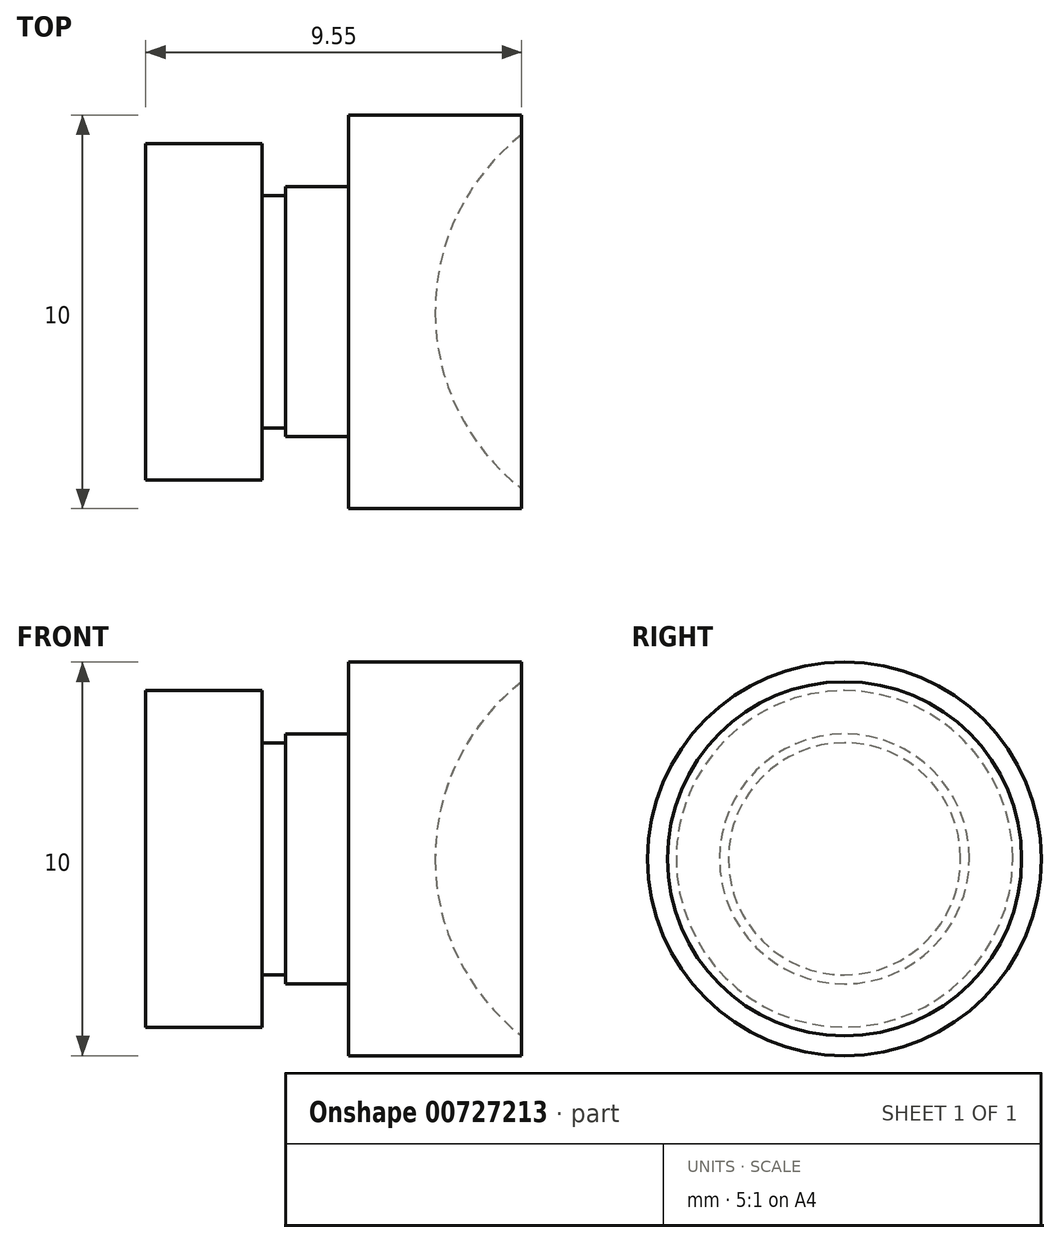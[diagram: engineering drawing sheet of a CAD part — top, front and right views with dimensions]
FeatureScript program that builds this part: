
annotation { "Feature Type Name" : "Feature", "Feature Type Description" : "" }
export const myFeature = defineFeature(function(context is Context, id is Id, definition is map)
    precondition{}
    {
        {
            var Q0;
            Q0=qCreatedBy(makeId("Right.planeOp"),FACE);
            var sketch = newSketch(context, id + "F0", { "sketchPlane" : qUnion([Q0])});
            skCircle(sketch, "E0", {"center": v(0, 0) * mm, "radius": 5 * mm});
            skSolve(sketch);
        }
        {
            var Q0;
            Q0 = qSketchRegion(id + "F0", true);
            extrude(context, id + "F1", {"entities" : qUnion([Q0]), "depth" : 4.4 * mm, "offsetDistance" : 25 * mm});
        }
        {
            var Q0;
            Q0=qCreatedBy(makeId("Right.planeOp"),FACE);
            var sketch = newSketch(context, id + "F2", { "sketchPlane" : qUnion([Q0])});
            skCircle(sketch, "E1", {"center": v(0, 0) * mm, "radius": 3.17 * mm});
            skSolve(sketch);
        }
        {
            var Q0;
            Q0 = qSketchRegion(id + "F2", true);
            extrude(context, id + "F3", {"entities" : qUnion([Q0]), "operationType" : NewBodyOperationType.ADD, "oppositeDirection" : true, "depth" : 1.6 * mm, "offsetDistance" : 25 * mm});
        }
        {
            var Q0;
            Q0=qCreatedBy(makeId("Right.planeOp"),FACE);
            cPlane(context, id + "F4", {"entities" : qUnion([Q0]), "cplaneType" : CPlaneType.OFFSET, "offset" : 1.6 * mm, "oppositeDirection" : true, "width" : 150 * mm, "height" : 150 * mm});
        }
        {
            var Q0;
            Q0=qCreatedBy(id+"F4.planeOp",FACE);
            var sketch = newSketch(context, id + "F5", { "sketchPlane" : qUnion([Q0])});
            skCircle(sketch, "E2", {"center": v(0, 0) * mm, "radius": 2.95 * mm});
            skSolve(sketch);
        }
        {
            var Q0;
            Q0 = qSketchRegion(id + "F5", true);
            extrude(context, id + "F6", {"entities" : qUnion([Q0]), "operationType" : NewBodyOperationType.ADD, "oppositeDirection" : true, "depth" : 0.6 * mm, "offsetDistance" : 25 * mm});
        }
        {
            var Q0;
            Q0=qCreatedBy(makeId("Right.planeOp"),FACE);
            cPlane(context, id + "F7", {"entities" : qUnion([Q0]), "cplaneType" : CPlaneType.OFFSET, "offset" : 2.2 * mm, "oppositeDirection" : true, "width" : 150 * mm, "height" : 150 * mm});
        }
        {
            var Q0;
            Q0=qCreatedBy(id+"F7.planeOp",FACE);
            var sketch = newSketch(context, id + "F8", { "sketchPlane" : qUnion([Q0])});
            skCircle(sketch, "E3", {"center": v(0, 0) * mm, "radius": 4.28 * mm});
            skSolve(sketch);
        }
        {
            var Q0;
            Q0 = qSketchRegion(id + "F8", true);
            extrude(context, id + "F9", {"entities" : qUnion([Q0]), "operationType" : NewBodyOperationType.ADD, "oppositeDirection" : true, "depth" : 2.95 * mm, "offsetDistance" : 25 * mm});
        }
        {
            var Q0;
            Q0=qCreatedBy(makeId("Front.planeOp"),FACE);
            var sketch = newSketch(context, id + "F10", { "sketchPlane" : qUnion([Q0])});
            skLineSegment(sketch, "E4.0", {"start": v(4.4, 5) * mm, "end": v(4.4, 4.5) * mm});
            skLineSegment(sketch, "E5", {"start": v(4.4, 4.5) * mm, "end": v(4.4, 0) * mm});
            skLineSegment(sketch, "E6", {"start": v(4.4, 0) * mm, "end": v(2.2, 0) * mm});
            skArc(sketch, "E7", {"start": v(4.4, 4.5) * mm, "mid": v(2.78, 2.5) * mm, "end": v(2.2, 0) * mm});
            skPoint(sketch, "E8.end.orphan", {"position": v(4.4, -5) * mm});
            skSolve(sketch);
        }
        {
            var Q0;
            Q0 = qSketchRegion(id + "F10", true);
            var Q1;
            Q1=sQuery(id+"F10.wireOp",EDGE,"E6");
            revolve(context, id + "F11", {"operationType" : NewBodyOperationType.REMOVE, "surfaceOperationType" : NewSurfaceOperationType.NEW, "entities" : qUnion([Q0]), "axis" : qUnion([Q1]), "revolveType" : RevolveType.FULL, "oppositeDirection" : true});
        }
    });
